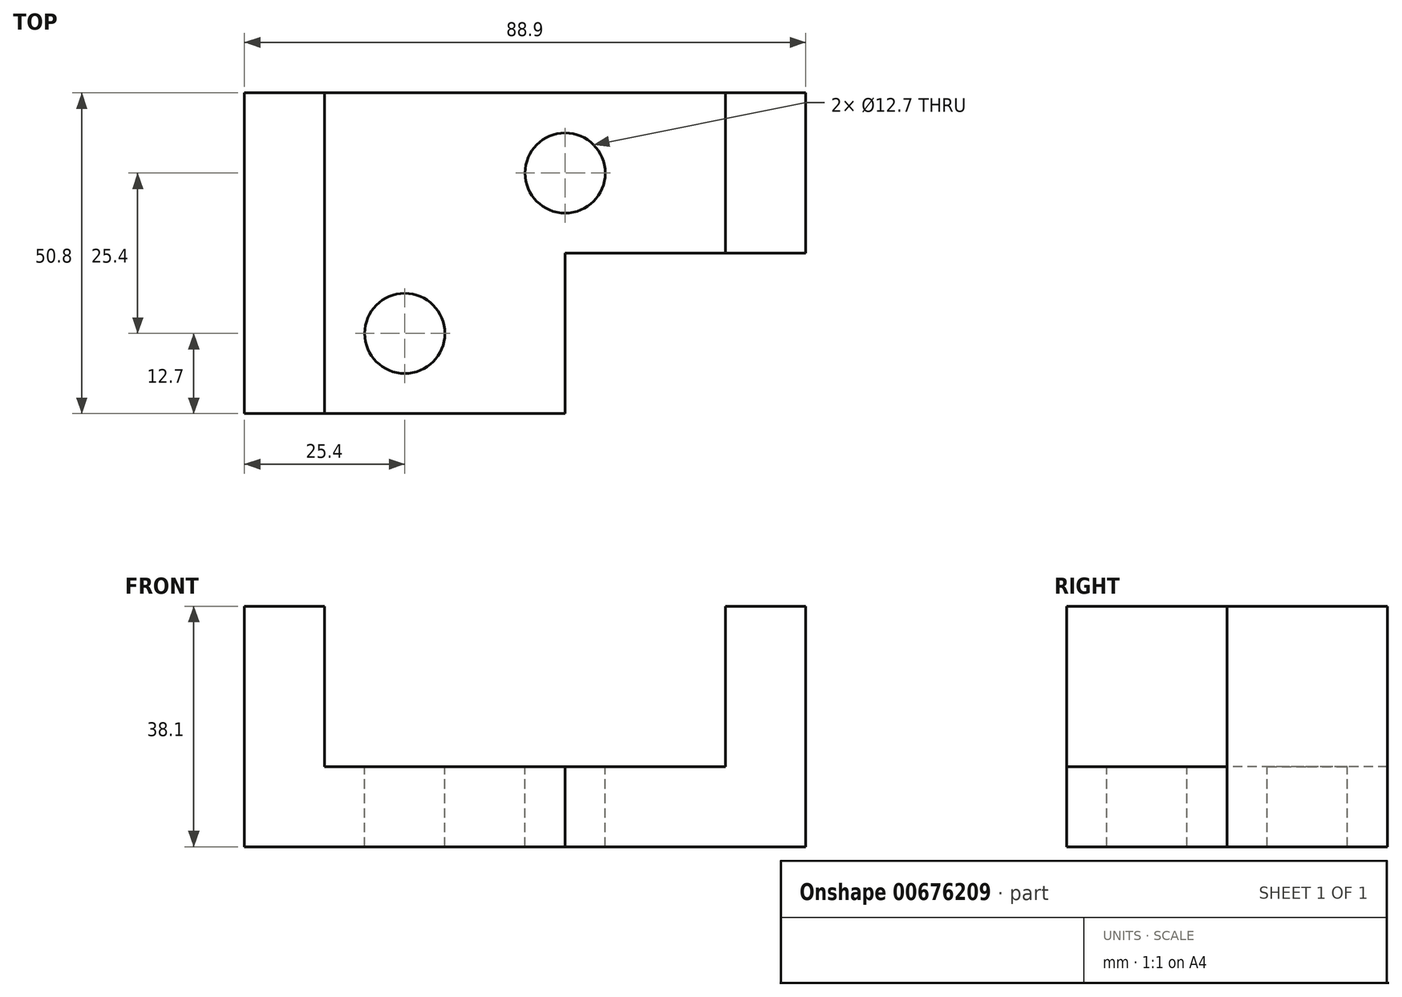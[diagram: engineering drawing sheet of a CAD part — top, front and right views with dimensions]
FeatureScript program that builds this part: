
annotation { "Feature Type Name" : "Feature", "Feature Type Description" : "" }
export const myFeature = defineFeature(function(context is Context, id is Id, definition is map)
    precondition{}
    {
        {
            var Q0;
            Q0=qCreatedBy(makeId("Front.planeOp"),FACE);
            var sketch = newSketch(context, id + "F0", { "sketchPlane" : qUnion([Q0])});
            skLineSegment(sketch, "E0.bottom", {"start": v(-44.45, -19.05) * mm, "end": v(44.45, -19.05) * mm});
            skLineSegment(sketch, "E0.top", {"start": v(-44.45, 19.05) * mm, "end": v(44.45, 19.05) * mm});
            skLineSegment(sketch, "E0.left", {"start": v(-44.45, -19.05) * mm, "end": v(-44.45, 19.05) * mm});
            skLineSegment(sketch, "E0.right", {"start": v(44.45, -19.05) * mm, "end": v(44.45, 19.05) * mm});
            skPoint(sketch, "E0.middle", {"position": v(0, 0) * mm});
            skSolve(sketch);
        }
        {
            var Q0;
            Q0 = qSketchRegion(id + "F0", true);
            extrude(context, id + "F1", {"entities" : qUnion([Q0]), "depth" : 50.8 * mm, "offsetDistance" : 25.4 * mm});
        }
        {
            var Q0;
            Q0=makeQuery(id+"F1.opExtrude","CAP_FACE",FACE,{"disambiguationData":[OSD([sQuery(id+"F0.wireOp",EDGE,"E0.bottom"),sQuery(id+"F0.wireOp",EDGE,"E0.top"),sQuery(id+"F0.wireOp",EDGE,"E0.left"),sQuery(id+"F0.wireOp",EDGE,"E0.right")])],"isStart":false});
            var sketch = newSketch(context, id + "F2", { "sketchPlane" : qUnion([Q0])});
            skLineSegment(sketch, "E1.bottom", {"start": v(-31.75, -6.35) * mm, "end": v(31.75, -6.35) * mm});
            skLineSegment(sketch, "E1.top", {"start": v(-31.75, 19.05) * mm, "end": v(31.75, 19.05) * mm});
            skLineSegment(sketch, "E1.left", {"start": v(-31.75, -6.35) * mm, "end": v(-31.75, 19.05) * mm});
            skLineSegment(sketch, "E1.right", {"start": v(31.75, -6.35) * mm, "end": v(31.75, 19.05) * mm});
            skSolve(sketch);
        }
        {
            var Q0;
            Q0 = qSketchRegion(id + "F2", true);
            extrude(context, id + "F3", {"entities" : qUnion([Q0]), "operationType" : NewBodyOperationType.REMOVE, "endBound" : BoundingType.THROUGH_ALL, "oppositeDirection" : true, "depth" : 25.4 * mm, "offsetDistance" : 25.4 * mm});
        }
        {
            var Q0;
            {var subQ0=sQuery(id+"F0.wireOp",EDGE,"E0.right");var subQ2=sQuery(id+"F0.wireOp",EDGE,"E0.top");Q0=makeQuery(id+"F3.boolean.opBoolean","SPLIT",FACE,{"disambiguationData":[TD([makeQuery(id+"F1.opExtrude","SWEPT_FACE",FACE,{"disambiguationData":[OSD([subQ0])]})])],"derivedFrom":makeQuery(id+"F1.opExtrude","SWEPT_FACE",FACE,{"disambiguationData":[OSD([subQ2])]})});}
            var sketch = newSketch(context, id + "F4", { "sketchPlane" : qUnion([Q0])});
            skLineSegment(sketch, "E2.bottom", {"start": v(44.45, -50.8) * mm, "end": v(6.35, -50.8) * mm});
            skLineSegment(sketch, "E2.top", {"start": v(44.45, -25.4) * mm, "end": v(6.35, -25.4) * mm});
            skLineSegment(sketch, "E2.left", {"start": v(44.45, -50.8) * mm, "end": v(44.45, -25.4) * mm});
            skLineSegment(sketch, "E2.right", {"start": v(6.35, -50.8) * mm, "end": v(6.35, -25.4) * mm});
            skSolve(sketch);
        }
        {
            var Q0;
            Q0 = qSketchRegion(id + "F4", true);
            extrude(context, id + "F5", {"entities" : qUnion([Q0]), "operationType" : NewBodyOperationType.REMOVE, "endBound" : BoundingType.THROUGH_ALL, "oppositeDirection" : true, "depth" : 25.4 * mm, "offsetDistance" : 25.4 * mm});
        }
        {
            var Q0;
            Q0=makeQuery(id+"F3.boolean.opBoolean","COPY",FACE,{"derivedFrom":makeQuery(id+"F3.opExtrude","SWEPT_FACE",FACE,{"disambiguationData":[OSD([sQuery(id+"F2.wireOp",EDGE,"E1.bottom")])]})});
            var sketch = newSketch(context, id + "F6", { "sketchPlane" : qUnion([Q0])});
            skCircle(sketch, "E3", {"center": v(6.35, -12.7) * mm, "radius": 6.35 * mm});
            skSolve(sketch);
        }
        {
            var Q0;
            Q0 = qSketchRegion(id + "F6", true);
            extrude(context, id + "F7", {"entities" : qUnion([Q0]), "operationType" : NewBodyOperationType.REMOVE, "endBound" : BoundingType.THROUGH_ALL, "oppositeDirection" : true, "depth" : 25.4 * mm, "offsetDistance" : 25.4 * mm});
        }
        {
            var Q0;
            Q0=makeQuery(id+"F3.boolean.opBoolean","COPY",FACE,{"derivedFrom":makeQuery(id+"F3.opExtrude","SWEPT_FACE",FACE,{"disambiguationData":[OSD([sQuery(id+"F2.wireOp",EDGE,"E1.bottom")])]})});
            var sketch = newSketch(context, id + "F8", { "sketchPlane" : qUnion([Q0])});
            skCircle(sketch, "E4", {"center": v(-19.05, -38.1) * mm, "radius": 6.35 * mm});
            skSolve(sketch);
        }
        {
            var Q0;
            Q0 = qSketchRegion(id + "F8", true);
            extrude(context, id + "F9", {"entities" : qUnion([Q0]), "operationType" : NewBodyOperationType.REMOVE, "endBound" : BoundingType.THROUGH_ALL, "oppositeDirection" : true, "depth" : 25.4 * mm, "offsetDistance" : 25.4 * mm});
        }
    });
